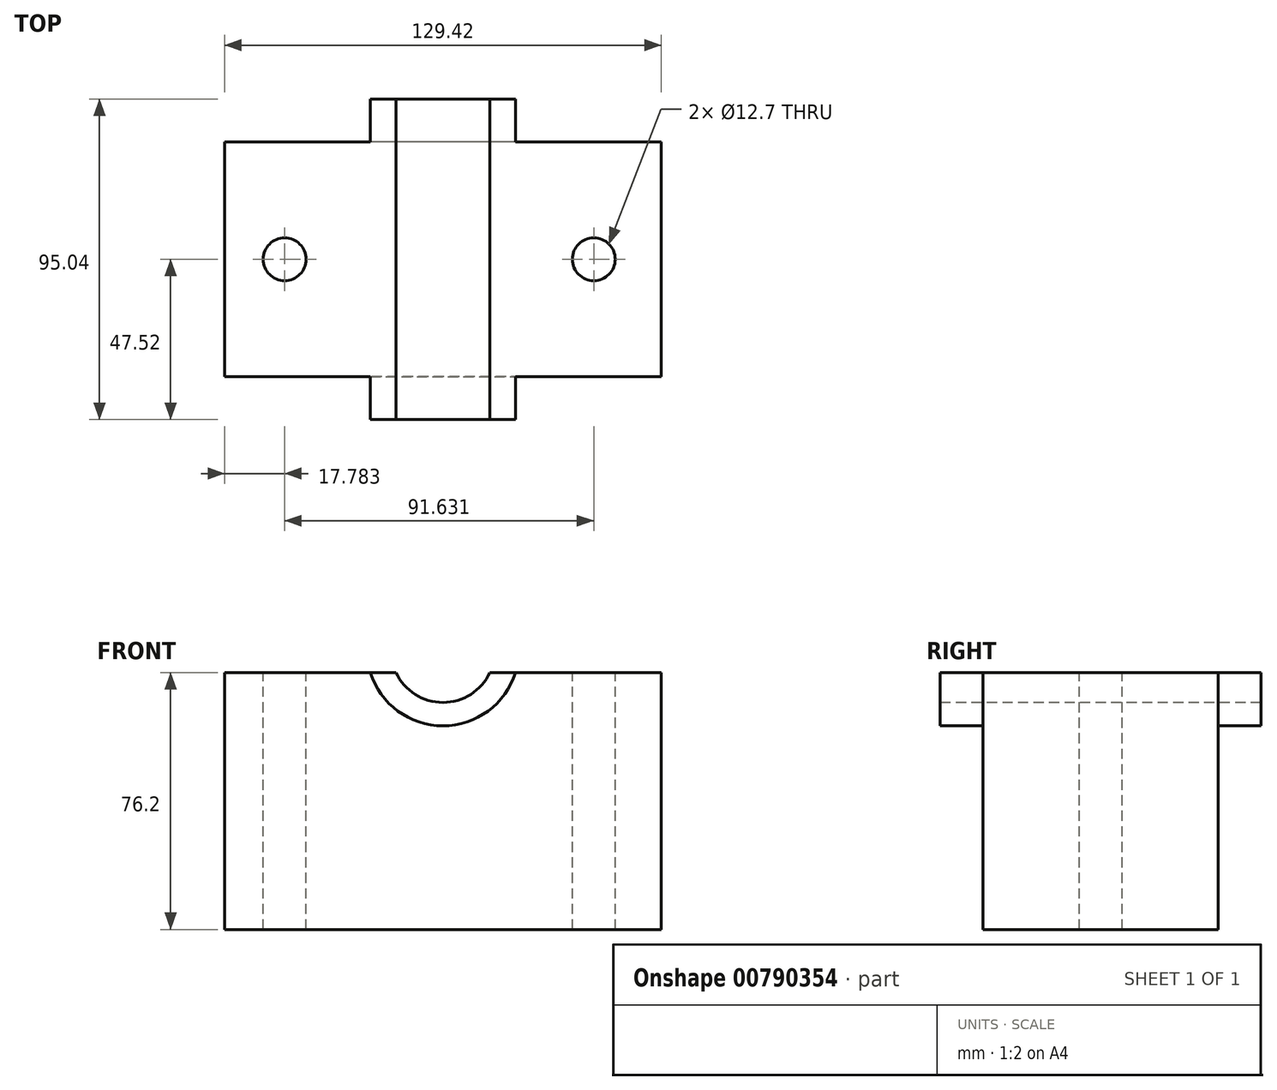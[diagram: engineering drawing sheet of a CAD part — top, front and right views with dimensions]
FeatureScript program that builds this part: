
annotation { "Feature Type Name" : "Feature", "Feature Type Description" : "" }
export const myFeature = defineFeature(function(context is Context, id is Id, definition is map)
    precondition{}
    {
        {
            var Q0;
            Q0=qCreatedBy(makeId("Top.planeOp"),FACE);
            var sketch = newSketch(context, id + "F0", { "sketchPlane" : qUnion([Q0])});
            skLineSegment(sketch, "E0.bottom", {"start": v(64.7, -34.82) * mm, "end": v(-64.7, -34.82) * mm});
            skLineSegment(sketch, "E0.top", {"start": v(64.7, 34.82) * mm, "end": v(-64.7, 34.82) * mm});
            skLineSegment(sketch, "E0.left", {"start": v(64.7, -34.82) * mm, "end": v(64.7, 34.82) * mm});
            skLineSegment(sketch, "E0.right", {"start": v(-64.7, -34.82) * mm, "end": v(-64.7, 34.82) * mm});
            skPoint(sketch, "E0.middle", {"position": v(0, 0) * mm});
            skSolve(sketch);
        }
        {
            var Q0;
            Q0=makeQuery(id+"F0.imprint","IMPRINT",FACE,{"disambiguationData":[TD([[makeQuery(id+"F0.imprint","IMPRINT",EDGE,{"derivedFrom":sQuery(id+"F0.wireOp",EDGE,"E0.bottom")}),-1.0]])]});
            extrude(context, id + "F1", {"entities" : qUnion([Q0]), "depth" : 76.2 * mm, "offsetDistance" : 25.4 * mm});
        }
        {
            var Q0;
            Q0=makeQuery(id+"F1.opExtrude","SWEPT_FACE",FACE,{"disambiguationData":[OSD([sQuery(id+"F0.wireOp",EDGE,"E0.top")])]});
            var sketch = newSketch(context, id + "F2", { "sketchPlane" : qUnion([Q0])});
            skLineSegment(sketch, "E1", {"start": v(-64.7, 76.2) * mm, "end": v(-13.9, 76.2) * mm});
            skLineSegment(sketch, "E2", {"start": v(64.7, 76.2) * mm, "end": v(13.9, 76.2) * mm});
            skArc(sketch, "E3", {"start": v(-13.9, 76.2) * mm, "mid": v(0, 67.31) * mm, "end": v(13.9, 76.2) * mm});
            skLineSegment(sketch, "E4", {"start": v(-64.7, 76.2) * mm, "end": v(-21.53, 76.2) * mm});
            skLineSegment(sketch, "E5", {"start": v(64.7, 76.2) * mm, "end": v(21.53, 76.2) * mm});
            skArc(sketch, "E6", {"start": v(-21.53, 76.2) * mm, "mid": v(0, 60.38) * mm, "end": v(21.53, 76.2) * mm});
            skSolve(sketch);
        }
        {
            var Q0;
            Q0=makeQuery(id+"F2.imprint","IMPRINT",FACE,{"disambiguationData":[TD([[makeQuery(id+"F2.imprint","IMPRINT",EDGE,{"derivedFrom":sQuery(id+"F2.wireOp",EDGE,"E1")}),-1.0]])]});
            extrude(context, id + "F3", {"entities" : qUnion([Q0]), "operationType" : NewBodyOperationType.ADD, "depth" : 12.7 * mm, "offsetDistance" : 25.4 * mm});
        }
        {
            var Q0;
            {var subQ0=sQuery(id+"F2.wireOp",EDGE,"E3");Q0=makeQuery(id+"F2.imprint","IMPRINT",FACE,{"disambiguationData":[TD([[makeQuery(id+"F2.imprint","IMPRINT",EDGE,{"derivedFrom":subQ0}),1.0]])]});}
            extrude(context, id + "F4", {"entities" : qUnion([Q0]), "operationType" : NewBodyOperationType.REMOVE, "oppositeDirection" : true, "depth" : 127 * mm, "offsetDistance" : 25.4 * mm});
        }
        {
            var Q0;
            Q0=makeQuery(id+"F1.opExtrude","SWEPT_FACE",FACE,{"disambiguationData":[OSD([sQuery(id+"F0.wireOp",EDGE,"E0.bottom")])]});
            var sketch = newSketch(context, id + "F5", { "sketchPlane" : qUnion([Q0])});
            skLineSegment(sketch, "E7", {"start": v(-64.7, 76.2) * mm, "end": v(-21.53, 76.2) * mm});
            skLineSegment(sketch, "E8", {"start": v(64.7, 76.2) * mm, "end": v(21.53, 76.2) * mm});
            skArc(sketch, "E9", {"start": v(-21.53, 76.2) * mm, "mid": v(0, 60.38) * mm, "end": v(21.53, 76.2) * mm});
            skSolve(sketch);
        }
        {
            var Q0;
            {var subQ0=sQuery(id+"F5.wireOp",EDGE,"E9");Q0=makeQuery(id+"F5.imprint","IMPRINT",FACE,{"disambiguationData":[TD([[makeQuery(id+"F5.imprint","IMPRINT",EDGE,{"derivedFrom":subQ0}),1.0]])]});}
            extrude(context, id + "F6", {"entities" : qUnion([Q0]), "operationType" : NewBodyOperationType.ADD, "depth" : 12.7 * mm, "offsetDistance" : 25.4 * mm});
        }
        {
            var Q0;
            {var subQ0=sQuery(id+"F2.wireOp",EDGE,"E1");var subQ1=makeQuery(id+"F3.opExtrude","SWEPT_FACE",FACE,{"disambiguationData":[OSD([subQ0])]});var subQ2=sQuery(id+"F0.wireOp",EDGE,"E0.right");var subQ3=sQuery(id+"F0.wireOp",EDGE,"E0.top");var subQ4=sQuery(id+"F0.wireOp",EDGE,"E0.bottom");var subQ5=makeQuery(id+"F1.opExtrude","CAP_FACE",FACE,{"disambiguationData":[OSD([subQ4,subQ3,sQuery(id+"F0.wireOp",EDGE,"E0.left"),subQ2])],"isStart":false});var subQ6=makeQuery(id+"F1.opExtrude","SWEPT_FACE",FACE,{"disambiguationData":[OSD([subQ2])]});var subQ7=sQuery(id+"F2.wireOp",EDGE,"E3");var subQ9=makeQuery(id+"F1.opExtrude","SWEPT_FACE",FACE,{"disambiguationData":[OSD([subQ4])]});var subQ10=sQuery(id+"F2.wireOp",EDGE,"E2");var subQ11=makeQuery(id+"F3.opExtrude","SWEPT_FACE",FACE,{"disambiguationData":[OSD([subQ10])]});var subQ12=makeQuery(id+"F4.opExtrude","SWEPT_FACE",FACE,{"disambiguationData":[OSD([subQ7])]});var subQ13=makeQuery(id+"F4.boolean.opBoolean","SPLIT",EDGE,{"disambiguationData":[TD([subQ6])],"derivedFrom":makeQuery(id+"F1.opExtrude","CAP_EDGE",EDGE,{"disambiguationData":[OSD([subQ4])],"isStart":false})});Q0=makeQuery(id+"F6.boolean.opBoolean","MERGE",FACE,{"derivedFrom":[makeQuery(id+"F4.boolean.opBoolean","SPLIT",FACE,{"disambiguationData":[TD([subQ6])],"derivedFrom":makeQuery(id+"F3.boolean.opBoolean","MERGE",FACE,{"derivedFrom":[subQ5,subQ1,subQ11]})}),makeQuery(id+"F6.opExtrude","SWEPT_FACE",FACE,{"disambiguationData":[OSD([subQ4]),TDD([makeQuery(id+"F5.imprint","IMPRINT",EDGE,{"disambiguationData":[TD([[makeQuery(id+"F5.imprint","INTERSECT",VERTEX,{"derivedFrom":[makeQuery(id+"F4.boolean.opBoolean","INTERSECT",EDGE,{"derivedFrom":[subQ9,subQ12]}),subQ13]}),-1.0]])],"derivedFrom":subQ13})])]})]});}
            var sketch = newSketch(context, id + "F7", { "sketchPlane" : qUnion([Q0])});
            skCircle(sketch, "E10", {"center": v(-46.93, 0) * mm, "radius": 6.35 * mm});
            skCircle(sketch, "E11", {"center": v(44.7, 0) * mm, "radius": 6.35 * mm});
            skPoint(sketch, "E12.orphan", {"position": v(-64.7, 0) * mm});
            skPoint(sketch, "E13.start.orphan", {"position": v(64.7, 0) * mm});
            skSolve(sketch);
        }
        {
            var Q0;
            Q0=makeQuery(id+"F7.imprint","IMPRINT",FACE,{"disambiguationData":[TD([[makeQuery(id+"F7.imprint","IMPRINT",EDGE,{"derivedFrom":sQuery(id+"F7.wireOp",EDGE,"E10")}),1.0]])]});
            var Q1;
            Q1=makeQuery(id+"F7.imprint","IMPRINT",FACE,{"disambiguationData":[TD([[makeQuery(id+"F7.imprint","IMPRINT",EDGE,{"derivedFrom":sQuery(id+"F7.wireOp",EDGE,"E11")}),1.0]])]});
            extrude(context, id + "F8", {"entities" : qUnion([Q0, Q1]), "operationType" : NewBodyOperationType.REMOVE, "oppositeDirection" : true, "depth" : 127 * mm, "offsetDistance" : 25.4 * mm});
        }
    });
